# Revit family: MBS_closet with drawer for basins
name_source: partatom
category: Generic Models
revit_build: Autodesk Revit 2014 (Build: 20130308_1515(x64)
units: mm (PartAtom-declared; Revit-internal decimal feet)

## types (1)
- kitchen closet for basin
    c_close door widht = 467 mm  [stored 1.53215 ft]
    c_closet back height = 820 mm  [stored 2.69029 ft]
    c_closet back widht = 934 mm  [stored 3.0643 ft]
    c_closet base depht = 540 mm  [stored 1.77165 ft]
    c_closet base widht = 874 mm  [stored 2.86745 ft]
    c_closet door height = 790 mm  [stored 2.59186 ft]
    c_closet side height = 820 mm  [stored 2.69029 ft]
    c_closet side widht = 540 mm  [stored 1.77165 ft]
    c_closet top depht = 540 mm  [stored 1.77165 ft]
    c_closet top widht = 874 mm  [stored 2.86745 ft]
    c_shelf depht = 540 mm  [stored 1.77165 ft]
    c_shelf widht = 874 mm  [stored 2.86745 ft]
    c_top depht = 75 mm
    c_top widht = 934 mm  [stored 3.0643 ft]
    closet with door material = Walnut KITCHEN CLOSET MBS
    panel thickness = 30 mm  [stored 0.0984252 ft]
    top material = Granite, Cut, Polished TOP MBS

note: [stored X ft] marks values corroborated as IEEE doubles in the binary element streams (Revit-internal decimal feet)

## geometry (parser evidence)
native form markers: Blend x4, Sweep x7
no freeform markers — native parametric forms only
